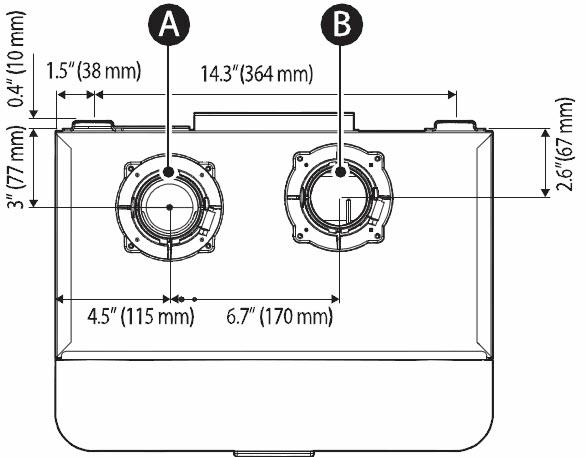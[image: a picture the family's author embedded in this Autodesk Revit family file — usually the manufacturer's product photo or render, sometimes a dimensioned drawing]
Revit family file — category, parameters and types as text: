
# Revit family: Water_Heater-Navien-NCB_Series
name_source: partatom
category: Mechanical Equipment
revit_build: Autodesk Revit MEP 2013 (Build: 20130531_2115(x64)
units: mm (PartAtom-declared; Revit-internal decimal feet)

## types (3) — shared parameters
Apparent Load = 0 VA
Auto Feeder = 1"
Cold Water Inlet = 1"
Default Elevation = 4' - 0"
Description = Condensing Gas Combination Boiler (NCB)
Enclosure = Metal - Navien - White
Exhaust = 3"
Frequency = 60 Hz
Gas Inlet = 1"
Height = 2' - 4"
Hot Water Outlet = 1"
Intake = 3"
Length = 1' - 0"
Manufacturer = Navien
Natural Gas Supply Pressure = 3.5 inches - 10.5 inches WC
Number of Poles = 1
Phase = 1
Power Factor = 1
Product Documentation Link = http://us.navien.com
Product Name = NCB
Product Page URL = http://us.navien.com
Propane Gas Supply Pressure = 8.0 inches - 13.5 inches WC
URL = http://us.navien.com
Voltage = 120 V
Water Pressure = 12-30 PSI / 15-150 PSI
Width = 1' - 5"

## per-type parameters (varying)
| type | Flow Rate | Heating Capacity | Model | Operating Weight |
| NCB 180 | 3.4 GPM | 80000.0 Btu/h | NCB - 180 | 74.00 lb |
| NCB 210 | 4.0 GPM | 100000.0 Btu/h | NCB - 210 | 84.00 lb |
| NCB 240 | 4.5 GPM | 120000.0 Btu/h | NCB - 240 | 84.00 lb |

## geometry (parser evidence)
native form markers: Blend x6, Sweep x3
no freeform markers — native parametric forms only
